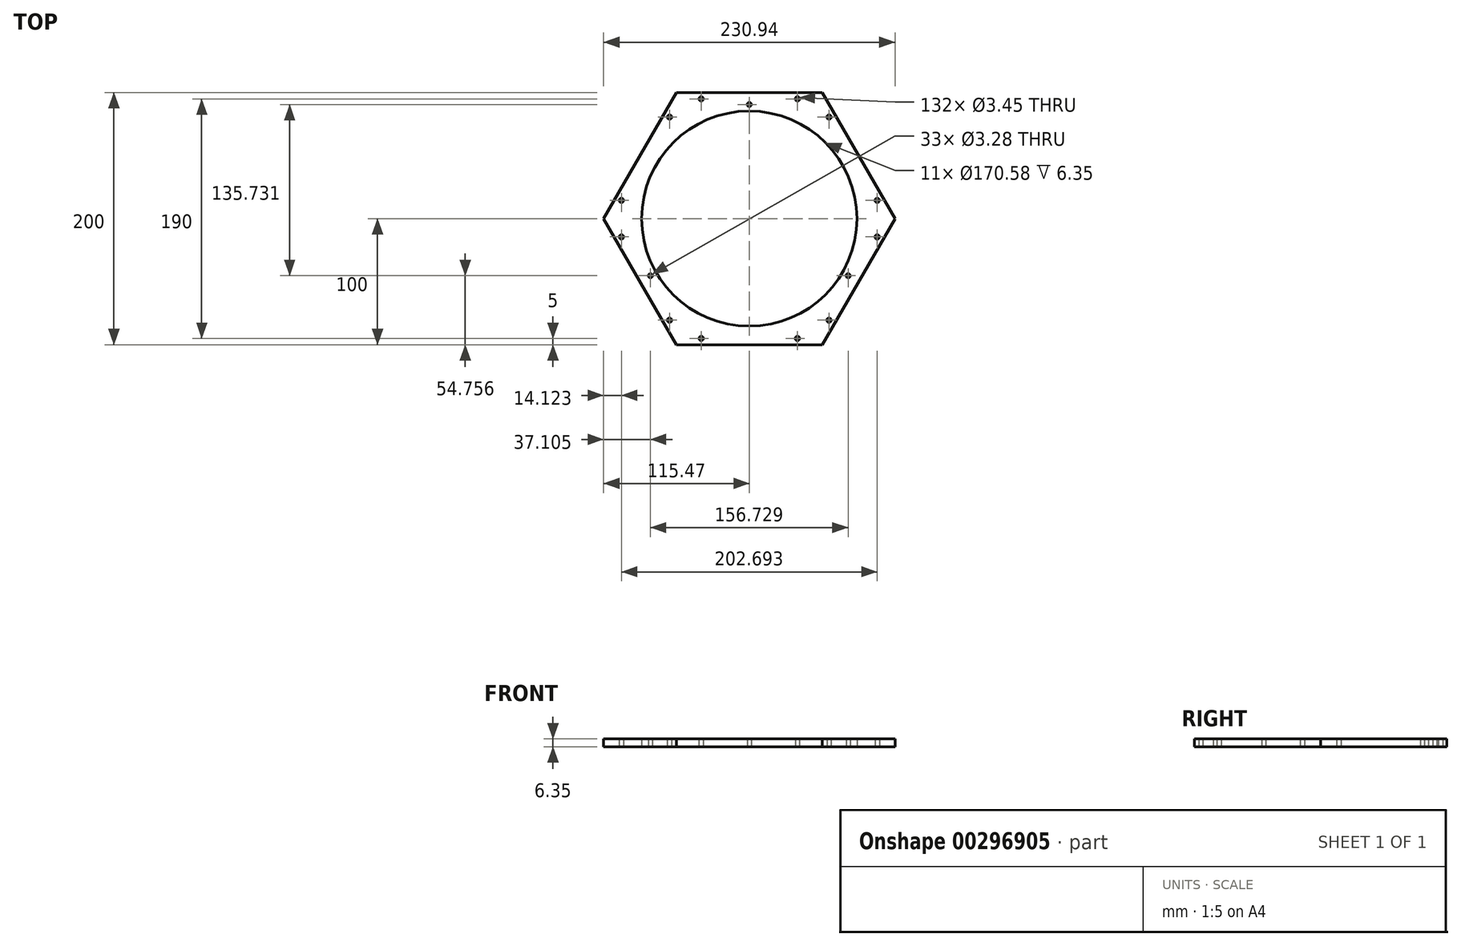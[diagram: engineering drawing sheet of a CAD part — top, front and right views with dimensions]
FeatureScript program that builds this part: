
annotation { "Feature Type Name" : "Feature", "Feature Type Description" : "" }
export const myFeature = defineFeature(function(context is Context, id is Id, definition is map)
    precondition{}
    {
        {
            var Q0;
            Q0=qCreatedBy(makeId("Top.planeOp"),FACE);
            var sketch = newSketch(context, id + "F0", { "sketchPlane" : qUnion([Q0])});
            skCircle(sketch, "E0", {"center": v(0, 0) * mm, "radius": 100 * mm});
            skCircle(sketch, "E1.cCircle", {"center": v(0, 0) * mm, "radius": 100 * mm, "construction": true});
            skLineSegment(sketch, "E1.0", {"start": v(-57.74, 100) * mm, "end": v(57.74, 100) * mm});
            skLineSegment(sketch, "E1.1", {"start": v(57.74, 100) * mm, "end": v(115.47, 0) * mm});
            skLineSegment(sketch, "E1.2", {"start": v(115.47, 0) * mm, "end": v(57.74, -100) * mm});
            skLineSegment(sketch, "E1.3", {"start": v(57.74, -100) * mm, "end": v(-57.74, -100) * mm});
            skLineSegment(sketch, "E1.4", {"start": v(-57.74, -100) * mm, "end": v(-115.47, 0) * mm});
            skLineSegment(sketch, "E1.5", {"start": v(-115.47, 0) * mm, "end": v(-57.74, 100) * mm});
            skPoint(sketch, "E1.0.midPoint", {"position": v(0, 100) * mm});
            skCircle(sketch, "E2", {"center": v(0, 0) * mm, "radius": 85.29 * mm});
            skCircle(sketch, "E3", {"center": v(0, 0) * mm, "radius": 75.29 * mm});
            skArc(sketch, "E4", {"start": v(-142.3, 0) * mm, "mid": v(-71.15, -123.24) * mm, "end": v(71.15, -123.24) * mm, "construction": true});
            skArc(sketch, "E5", {"start": v(-142.3, 0) * mm, "mid": v(-71.15, 123.24) * mm, "end": v(71.15, 123.24) * mm, "construction": true});
            skLineSegment(sketch, "E6", {"start": v(42.64, -73.86) * mm, "end": v(45.4, -72.27) * mm});
            skLineSegment(sketch, "E7", {"start": v(42.64, 73.86) * mm, "end": v(45.4, 72.27) * mm});
            skLineSegment(sketch, "E8", {"start": v(45.4, 72.27) * mm, "end": v(42.64, 73.86) * mm});
            skLineSegment(sketch, "E9", {"start": v(42.64, 73.86) * mm, "end": v(39.9, 75.45) * mm});
            skLineSegment(sketch, "E10", {"start": v(-85.29, 0) * mm, "end": v(-85.29, 3.18) * mm});
            skLineSegment(sketch, "E11", {"start": v(-85.29, 0) * mm, "end": v(-85.29, -3.18) * mm});
            skLineSegment(sketch, "E12", {"start": v(42.64, -73.86) * mm, "end": v(39.9, -75.45) * mm});
            skCircle(sketch, "E13", {"center": v(0, 0) * mm, "radius": 90.49 * mm, "construction": true});
            skLineSegment(sketch, "E14", {"start": v(0, 100) * mm, "end": v(0, 90.49) * mm, "construction": true});
            skLineSegment(sketch, "E15", {"start": v(86.6, -50) * mm, "end": v(78.36, -45.24) * mm, "construction": true});
            skLineSegment(sketch, "E16", {"start": v(-86.6, -50) * mm, "end": v(-78.36, -45.24) * mm, "construction": true});
            skCircle(sketch, "E17", {"center": v(0, 90.49) * mm, "radius": 1.64 * mm});
            skCircle(sketch, "E18", {"center": v(78.36, -45.24) * mm, "radius": 1.64 * mm});
            skCircle(sketch, "E19", {"center": v(-78.36, -45.24) * mm, "radius": 1.64 * mm});
            skSolve(sketch);
        }
        {
            var Q0;
            Q0=qSketchRegion(id+"F0",true);
            extrude(context, id + "F1", {"entities" : qUnion([Q0]), "depth" : 6.35 * mm});
        }
        {
            var Q0;
            Q0=qCreatedBy(makeId("Top.planeOp"),FACE);
            var sketch = newSketch(context, id + "F2", { "sketchPlane" : qUnion([Q0])});
            skCircle(sketch, "E20.cCircle", {"center": v(0, 0) * mm, "radius": 95 * mm, "construction": true});
            skLineSegment(sketch, "E20.0", {"start": v(-54.85, 95) * mm, "end": v(54.85, 95) * mm, "construction": true});
            skLineSegment(sketch, "E20.1", {"start": v(54.85, 95) * mm, "end": v(109.7, 0) * mm, "construction": true});
            skLineSegment(sketch, "E20.2", {"start": v(109.7, 0) * mm, "end": v(54.85, -95) * mm, "construction": true});
            skLineSegment(sketch, "E20.3", {"start": v(54.85, -95) * mm, "end": v(-54.85, -95) * mm, "construction": true});
            skLineSegment(sketch, "E20.4", {"start": v(-54.85, -95) * mm, "end": v(-109.7, 0) * mm, "construction": true});
            skLineSegment(sketch, "E20.5", {"start": v(-109.7, 0) * mm, "end": v(-54.85, 95) * mm, "construction": true});
            skPoint(sketch, "E20.0.midPoint", {"position": v(0, 95) * mm});
            skPoint(sketch, "E21", {"position": v(38.15, 95) * mm});
            skPoint(sketch, "E22", {"position": v(-38.15, 95) * mm});
            skPoint(sketch, "E23", {"position": v(38.15, -95) * mm});
            skPoint(sketch, "E24", {"position": v(-38.15, -95) * mm});
            skPoint(sketch, "E25", {"position": v(-63.2, -80.54) * mm});
            skPoint(sketch, "E26", {"position": v(-101.35, -14.46) * mm});
            skPoint(sketch, "E27", {"position": v(-101.35, 14.46) * mm});
            skPoint(sketch, "E28", {"position": v(-63.2, 80.54) * mm});
            skPoint(sketch, "E29", {"position": v(63.2, 80.54) * mm});
            skPoint(sketch, "E30", {"position": v(101.35, 14.46) * mm});
            skPoint(sketch, "E31", {"position": v(101.35, -14.46) * mm});
            skPoint(sketch, "E32", {"position": v(63.2, -80.54) * mm});
            skCircle(sketch, "E33", {"center": v(38.15, 95) * mm, "radius": 1.73 * mm});
            skCircle(sketch, "E34", {"center": v(-38.15, 95) * mm, "radius": 1.73 * mm});
            skCircle(sketch, "E35", {"center": v(-63.2, 80.54) * mm, "radius": 1.73 * mm});
            skCircle(sketch, "E36", {"center": v(-101.35, 14.46) * mm, "radius": 1.73 * mm});
            skCircle(sketch, "E37", {"center": v(-101.35, -14.46) * mm, "radius": 1.73 * mm});
            skCircle(sketch, "E38", {"center": v(-63.2, -80.54) * mm, "radius": 1.73 * mm});
            skCircle(sketch, "E39", {"center": v(-38.15, -95) * mm, "radius": 1.73 * mm});
            skCircle(sketch, "E40", {"center": v(38.15, -95) * mm, "radius": 1.73 * mm});
            skCircle(sketch, "E41", {"center": v(63.2, -80.54) * mm, "radius": 1.73 * mm});
            skCircle(sketch, "E42", {"center": v(101.35, -14.46) * mm, "radius": 1.73 * mm});
            skCircle(sketch, "E43", {"center": v(101.35, 14.46) * mm, "radius": 1.73 * mm});
            skCircle(sketch, "E44", {"center": v(63.2, 80.54) * mm, "radius": 1.73 * mm});
            skPoint(sketch, "E45.0.midPoint", {"position": v(0, 90) * mm});
            skSolve(sketch);
        }
        {
            var Q0;
            Q0 = qSketchRegion(id + "F2", true);
            extrude(context, id + "F3", {"entities" : qUnion([Q0]), "operationType" : NewBodyOperationType.REMOVE, "depth" : 25 * mm});
        }
    });
